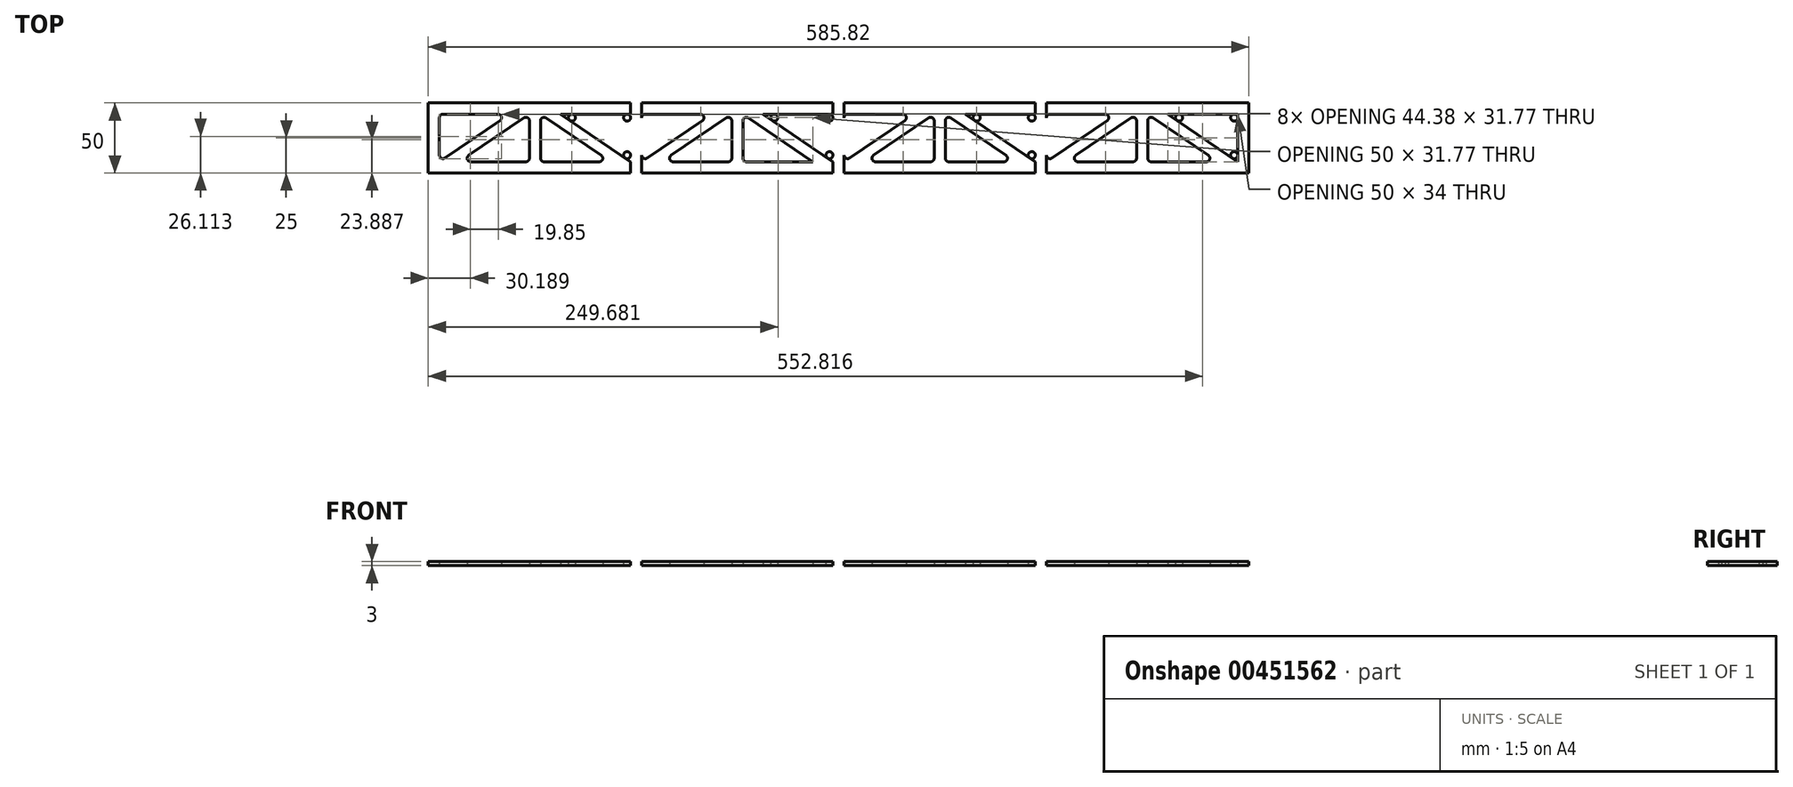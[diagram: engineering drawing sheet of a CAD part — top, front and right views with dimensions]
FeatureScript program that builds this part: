
annotation { "Feature Type Name" : "Feature", "Feature Type Description" : "" }
export const myFeature = defineFeature(function(context is Context, id is Id, definition is map)
    precondition{}
    {
        {
            var Q0;
            Q0=qCreatedBy(makeId("Top.planeOp"),FACE);
            var sketch = newSketch(context, id + "F0", { "sketchPlane" : qUnion([Q0])});
            skLineSegment(sketch, "E0.bottom", {"start": v(0, 0) * mm, "end": v(76.23, 0) * mm});
            skLineSegment(sketch, "E0.top", {"start": v(0, -50) * mm, "end": v(76.23, -50) * mm});
            skLineSegment(sketch, "E0.left", {"start": v(0, 0) * mm, "end": v(0, -50) * mm});
            skLineSegment(sketch, "E0.right", {"start": v(76.23, 0) * mm, "end": v(76.23, -50) * mm});
            skLineSegment(sketch, "E1", {"start": v(8, -8) * mm, "end": v(58, -8) * mm});
            skLineSegment(sketch, "E2", {"start": v(58, -8) * mm, "end": v(8, -42) * mm});
            skLineSegment(sketch, "E3", {"start": v(8, -42) * mm, "end": v(8, -8) * mm});
            skCircle(sketch, "E4", {"center": v(49.88, -10.5) * mm, "radius": 2.5 * mm});
            skCircle(sketch, "E5", {"center": v(10.5, -10.5) * mm, "radius": 2.5 * mm});
            skCircle(sketch, "E6", {"center": v(10.5, -37.28) * mm, "radius": 2.5 * mm});
            skLineSegment(sketch, "E7.MirrorCS", {"start": v(72.23, -8) * mm, "end": v(22.23, -42) * mm});
            skCircle(sketch, "E8.MirrorC", {"center": v(69.73, -12.72) * mm, "radius": 2.5 * mm});
            skLineSegment(sketch, "E9.MirrorCS", {"start": v(72.23, -42) * mm, "end": v(72.23, -8) * mm});
            skCircle(sketch, "E10.MirrorC", {"center": v(69.73, -39.5) * mm, "radius": 2.5 * mm});
            skCircle(sketch, "E11.MirrorC", {"center": v(30.35, -39.5) * mm, "radius": 2.5 * mm});
            skLineSegment(sketch, "E12.MirrorCS", {"start": v(22.23, -42) * mm, "end": v(72.23, -42) * mm});
            skCircle(sketch, "E13.MirrorC", {"center": v(141.95, -10.5) * mm, "radius": 2.5 * mm});
            skCircle(sketch, "E14.MirrorC", {"center": v(102.58, -10.5) * mm, "radius": 2.5 * mm});
            skCircle(sketch, "E15.MirrorC", {"center": v(141.95, -37.28) * mm, "radius": 2.5 * mm});
            skLineSegment(sketch, "E16.MirrorCS", {"start": v(144.45, -42) * mm, "end": v(144.45, -8) * mm});
            skLineSegment(sketch, "E17.MirrorCS", {"start": v(94.45, -8) * mm, "end": v(144.45, -42) * mm});
            skLineSegment(sketch, "E18.MirrorCS", {"start": v(144.45, -8) * mm, "end": v(94.45, -8) * mm});
            skCircle(sketch, "E19.MirrorC", {"center": v(82.73, -12.72) * mm, "radius": 2.5 * mm});
            skLineSegment(sketch, "E20.MirrorCS", {"start": v(130.23, -42) * mm, "end": v(80.23, -42) * mm});
            skLineSegment(sketch, "E21.MirrorCS", {"start": v(80.23, -8) * mm, "end": v(130.23, -42) * mm});
            skLineSegment(sketch, "E22.MirrorCS", {"start": v(152.45, 0) * mm, "end": v(152.45, -50) * mm});
            skCircle(sketch, "E23.MirrorC", {"center": v(82.73, -39.5) * mm, "radius": 2.5 * mm});
            skCircle(sketch, "E24.MirrorC", {"center": v(122.1, -39.5) * mm, "radius": 2.5 * mm});
            skLineSegment(sketch, "E25.MirrorCS", {"start": v(80.23, -42) * mm, "end": v(80.23, -8) * mm});
            skLineSegment(sketch, "E26.MirrorCS", {"start": v(152.45, -50) * mm, "end": v(76.23, -50) * mm});
            skLineSegment(sketch, "E27.MirrorCS", {"start": v(152.45, 0) * mm, "end": v(76.23, 0) * mm});
            skLineSegment(sketch, "E28.bottom", {"start": v(144.45, 0) * mm, "end": v(220.68, 0) * mm});
            skLineSegment(sketch, "E28.top", {"start": v(144.45, -50) * mm, "end": v(220.68, -50) * mm});
            skLineSegment(sketch, "E28.left", {"start": v(144.45, 0) * mm, "end": v(144.45, -50) * mm});
            skLineSegment(sketch, "E28.right", {"start": v(220.68, 0) * mm, "end": v(220.68, -50) * mm});
            skLineSegment(sketch, "E29", {"start": v(152.45, -8) * mm, "end": v(202.45, -8) * mm});
            skLineSegment(sketch, "E30", {"start": v(202.45, -8) * mm, "end": v(152.45, -42) * mm});
            skLineSegment(sketch, "E31", {"start": v(152.45, -42) * mm, "end": v(152.45, -8) * mm});
            skCircle(sketch, "E32", {"center": v(194.33, -10.5) * mm, "radius": 2.5 * mm});
            skCircle(sketch, "E33", {"center": v(154.95, -10.5) * mm, "radius": 2.5 * mm});
            skCircle(sketch, "E34", {"center": v(154.95, -37.28) * mm, "radius": 2.5 * mm});
            skLineSegment(sketch, "E35.MirrorCS", {"start": v(216.68, -8) * mm, "end": v(166.68, -42) * mm});
            skCircle(sketch, "E36.MirrorC", {"center": v(214.18, -12.72) * mm, "radius": 2.5 * mm});
            skLineSegment(sketch, "E37.MirrorCS", {"start": v(216.68, -42) * mm, "end": v(216.68, -8) * mm});
            skCircle(sketch, "E38.MirrorC", {"center": v(214.18, -39.5) * mm, "radius": 2.5 * mm});
            skCircle(sketch, "E39.MirrorC", {"center": v(174.8, -39.5) * mm, "radius": 2.5 * mm});
            skLineSegment(sketch, "E40.MirrorCS", {"start": v(166.68, -42) * mm, "end": v(216.68, -42) * mm});
            skCircle(sketch, "E41.MirrorC", {"center": v(286.4, -10.5) * mm, "radius": 2.5 * mm});
            skCircle(sketch, "E42.MirrorC", {"center": v(247.03, -10.5) * mm, "radius": 2.5 * mm});
            skCircle(sketch, "E43.MirrorC", {"center": v(286.4, -37.28) * mm, "radius": 2.5 * mm});
            skLineSegment(sketch, "E44.MirrorCS", {"start": v(288.9, -42) * mm, "end": v(288.9, -8) * mm});
            skLineSegment(sketch, "E45.MirrorCS", {"start": v(238.9, -8) * mm, "end": v(288.9, -42) * mm});
            skLineSegment(sketch, "E46.MirrorCS", {"start": v(288.9, -8) * mm, "end": v(238.9, -8) * mm});
            skCircle(sketch, "E47.MirrorC", {"center": v(227.18, -12.72) * mm, "radius": 2.5 * mm});
            skLineSegment(sketch, "E48.MirrorCS", {"start": v(274.68, -42) * mm, "end": v(224.68, -42) * mm});
            skLineSegment(sketch, "E49.MirrorCS", {"start": v(224.68, -8) * mm, "end": v(274.68, -42) * mm});
            skLineSegment(sketch, "E50.MirrorCS", {"start": v(296.9, 0) * mm, "end": v(296.9, -50) * mm});
            skCircle(sketch, "E51.MirrorC", {"center": v(227.18, -39.5) * mm, "radius": 2.5 * mm});
            skCircle(sketch, "E52.MirrorC", {"center": v(266.56, -39.5) * mm, "radius": 2.5 * mm});
            skLineSegment(sketch, "E53.MirrorCS", {"start": v(224.68, -42) * mm, "end": v(224.68, -8) * mm});
            skLineSegment(sketch, "E54.MirrorCS", {"start": v(296.9, -50) * mm, "end": v(220.68, -50) * mm});
            skLineSegment(sketch, "E55.MirrorCS", {"start": v(296.9, 0) * mm, "end": v(220.68, 0) * mm});
            skLineSegment(sketch, "E56.bottom", {"start": v(288.9, 0) * mm, "end": v(365.14, 0) * mm});
            skLineSegment(sketch, "E56.top", {"start": v(288.9, -50) * mm, "end": v(365.14, -50) * mm});
            skLineSegment(sketch, "E56.left", {"start": v(288.9, 0) * mm, "end": v(288.9, -50) * mm});
            skLineSegment(sketch, "E56.right", {"start": v(365.14, 0) * mm, "end": v(365.14, -50) * mm});
            skLineSegment(sketch, "E57", {"start": v(296.9, -8) * mm, "end": v(346.9, -8) * mm});
            skLineSegment(sketch, "E58", {"start": v(346.9, -8) * mm, "end": v(296.9, -42) * mm});
            skLineSegment(sketch, "E59", {"start": v(296.9, -42) * mm, "end": v(296.9, -8) * mm});
            skCircle(sketch, "E60", {"center": v(338.79, -10.5) * mm, "radius": 2.5 * mm});
            skCircle(sketch, "E61", {"center": v(299.4, -10.5) * mm, "radius": 2.5 * mm});
            skCircle(sketch, "E62", {"center": v(299.4, -37.28) * mm, "radius": 2.5 * mm});
            skLineSegment(sketch, "E63.MirrorCS", {"start": v(361.14, -8) * mm, "end": v(311.14, -42) * mm});
            skCircle(sketch, "E64.MirrorC", {"center": v(358.64, -12.72) * mm, "radius": 2.5 * mm});
            skLineSegment(sketch, "E65.MirrorCS", {"start": v(361.14, -42) * mm, "end": v(361.14, -8) * mm});
            skCircle(sketch, "E66.MirrorC", {"center": v(358.64, -39.5) * mm, "radius": 2.5 * mm});
            skCircle(sketch, "E67.MirrorC", {"center": v(319.26, -39.5) * mm, "radius": 2.5 * mm});
            skLineSegment(sketch, "E68.MirrorCS", {"start": v(311.14, -42) * mm, "end": v(361.14, -42) * mm});
            skCircle(sketch, "E69.MirrorC", {"center": v(430.86, -10.5) * mm, "radius": 2.5 * mm});
            skCircle(sketch, "E70.MirrorC", {"center": v(391.48, -10.5) * mm, "radius": 2.5 * mm});
            skCircle(sketch, "E71.MirrorC", {"center": v(430.86, -37.28) * mm, "radius": 2.5 * mm});
            skLineSegment(sketch, "E72.MirrorCS", {"start": v(433.36, -42) * mm, "end": v(433.36, -8) * mm});
            skLineSegment(sketch, "E73.MirrorCS", {"start": v(383.36, -8) * mm, "end": v(433.36, -42) * mm});
            skLineSegment(sketch, "E74.MirrorCS", {"start": v(433.36, -8) * mm, "end": v(383.36, -8) * mm});
            skCircle(sketch, "E75.MirrorC", {"center": v(371.64, -12.72) * mm, "radius": 2.5 * mm});
            skLineSegment(sketch, "E76.MirrorCS", {"start": v(419.14, -42) * mm, "end": v(369.14, -42) * mm});
            skLineSegment(sketch, "E77.MirrorCS", {"start": v(369.14, -8) * mm, "end": v(419.14, -42) * mm});
            skLineSegment(sketch, "E78.MirrorCS", {"start": v(441.36, 0) * mm, "end": v(441.36, -50) * mm});
            skCircle(sketch, "E79.MirrorC", {"center": v(371.64, -39.5) * mm, "radius": 2.5 * mm});
            skCircle(sketch, "E80.MirrorC", {"center": v(411.01, -39.5) * mm, "radius": 2.5 * mm});
            skLineSegment(sketch, "E81.MirrorCS", {"start": v(369.14, -42) * mm, "end": v(369.14, -8) * mm});
            skLineSegment(sketch, "E82.MirrorCS", {"start": v(441.36, -50) * mm, "end": v(365.14, -50) * mm});
            skLineSegment(sketch, "E83.MirrorCS", {"start": v(441.36, 0) * mm, "end": v(365.14, 0) * mm});
            skLineSegment(sketch, "E84.bottom", {"start": v(433.36, 0) * mm, "end": v(509.59, 0) * mm});
            skLineSegment(sketch, "E84.top", {"start": v(433.36, -50) * mm, "end": v(509.59, -50) * mm});
            skLineSegment(sketch, "E84.left", {"start": v(433.36, 0) * mm, "end": v(433.36, -50) * mm});
            skLineSegment(sketch, "E84.right", {"start": v(509.59, 0) * mm, "end": v(509.59, -50) * mm});
            skLineSegment(sketch, "E85", {"start": v(441.36, -8) * mm, "end": v(491.36, -8) * mm});
            skLineSegment(sketch, "E86", {"start": v(491.36, -8) * mm, "end": v(441.36, -42) * mm});
            skLineSegment(sketch, "E87", {"start": v(441.36, -42) * mm, "end": v(441.36, -8) * mm});
            skCircle(sketch, "E88", {"center": v(483.24, -10.5) * mm, "radius": 2.5 * mm});
            skCircle(sketch, "E89", {"center": v(443.86, -10.5) * mm, "radius": 2.5 * mm});
            skCircle(sketch, "E90", {"center": v(443.86, -37.28) * mm, "radius": 2.5 * mm});
            skLineSegment(sketch, "E91.MirrorCS", {"start": v(505.59, -8) * mm, "end": v(455.59, -42) * mm});
            skCircle(sketch, "E92.MirrorC", {"center": v(503.09, -12.72) * mm, "radius": 2.5 * mm});
            skLineSegment(sketch, "E93.MirrorCS", {"start": v(505.59, -42) * mm, "end": v(505.59, -8) * mm});
            skCircle(sketch, "E94.MirrorC", {"center": v(503.09, -39.5) * mm, "radius": 2.5 * mm});
            skCircle(sketch, "E95.MirrorC", {"center": v(463.71, -39.5) * mm, "radius": 2.5 * mm});
            skLineSegment(sketch, "E96.MirrorCS", {"start": v(455.59, -42) * mm, "end": v(505.59, -42) * mm});
            skCircle(sketch, "E97.MirrorC", {"center": v(575.32, -10.5) * mm, "radius": 2.5 * mm});
            skCircle(sketch, "E98.MirrorC", {"center": v(535.94, -10.5) * mm, "radius": 2.5 * mm});
            skCircle(sketch, "E99.MirrorC", {"center": v(575.32, -37.28) * mm, "radius": 2.5 * mm});
            skLineSegment(sketch, "E100.MirrorCS", {"start": v(577.82, -42) * mm, "end": v(577.82, -8) * mm});
            skLineSegment(sketch, "E101.MirrorCS", {"start": v(527.82, -8) * mm, "end": v(577.82, -42) * mm});
            skLineSegment(sketch, "E102.MirrorCS", {"start": v(577.82, -8) * mm, "end": v(527.82, -8) * mm});
            skCircle(sketch, "E103.MirrorC", {"center": v(516.09, -12.72) * mm, "radius": 2.5 * mm});
            skLineSegment(sketch, "E104.MirrorCS", {"start": v(563.59, -42) * mm, "end": v(513.59, -42) * mm});
            skLineSegment(sketch, "E105.MirrorCS", {"start": v(513.59, -8) * mm, "end": v(563.59, -42) * mm});
            skLineSegment(sketch, "E106.MirrorCS", {"start": v(585.82, 0) * mm, "end": v(585.82, -50) * mm});
            skCircle(sketch, "E107.MirrorC", {"center": v(516.09, -39.5) * mm, "radius": 2.5 * mm});
            skCircle(sketch, "E108.MirrorC", {"center": v(555.47, -39.5) * mm, "radius": 2.5 * mm});
            skLineSegment(sketch, "E109.MirrorCS", {"start": v(513.59, -42) * mm, "end": v(513.59, -8) * mm});
            skLineSegment(sketch, "E110.MirrorCS", {"start": v(585.82, -50) * mm, "end": v(509.59, -50) * mm});
            skLineSegment(sketch, "E111.MirrorCS", {"start": v(585.82, 0) * mm, "end": v(509.59, 0) * mm});
            skSolve(sketch);
        }
        {
            var Q0;
            Q0=makeQuery(id+"F0.imprint","IMPRINT",FACE,{"disambiguationData":[TD([[makeQuery(id+"F0.imprint","IMPRINT",EDGE,{"derivedFrom":sQuery(id+"F0.wireOp",EDGE,"E0.right")}),1.0]])]});
            var Q1;
            Q1=makeQuery(id+"F0.imprint","IMPRINT",FACE,{"disambiguationData":[TD([[makeQuery(id+"F0.imprint","IMPRINT",EDGE,{"derivedFrom":sQuery(id+"F0.wireOp",EDGE,"E0.bottom")}),-1.0]])]});
            var Q2;
            {var subQ0=sQuery(id+"F0.wireOp",EDGE,"E16.MirrorCS");var subQ1=sQuery(id+"F0.wireOp",EDGE,"E13.MirrorC");var subQ2=makeQuery(id+"F0.imprint","INTERSECT",VERTEX,{"derivedFrom":[subQ1,subQ0]});Q2=makeQuery(id+"F0.imprint","IMPRINT",FACE,{"disambiguationData":[TD([[makeQuery(id+"F0.imprint","IMPRINT",EDGE,{"disambiguationData":[TD([[subQ2,1.0]])],"derivedFrom":subQ1}),1.0]])]});}
            var Q3;
            {var subQ0=sQuery(id+"F0.wireOp",EDGE,"E16.MirrorCS");var subQ1=sQuery(id+"F0.wireOp",EDGE,"E15.MirrorC");var subQ2=makeQuery(id+"F0.imprint","INTERSECT",VERTEX,{"derivedFrom":[subQ1,subQ0]});Q3=makeQuery(id+"F0.imprint","IMPRINT",FACE,{"disambiguationData":[TD([[makeQuery(id+"F0.imprint","IMPRINT",EDGE,{"disambiguationData":[TD([[subQ2,-1.0]])],"derivedFrom":subQ1}),1.0]])]});}
            var Q4;
            {var subQ0=sQuery(id+"F0.wireOp",EDGE,"E21.MirrorCS");var subQ1=sQuery(id+"F0.wireOp",EDGE,"E20.MirrorCS");var subQ2=makeQuery(id+"F0.imprint","INTERSECT",VERTEX,{"derivedFrom":[subQ1,subQ0]});Q4=makeQuery(id+"F0.imprint","IMPRINT",FACE,{"disambiguationData":[TD([[makeQuery(id+"F0.imprint","IMPRINT",EDGE,{"disambiguationData":[TD([[subQ2,-1.0]])],"derivedFrom":subQ1}),-1.0]])]});}
            var Q5;
            {var subQ0=sQuery(id+"F0.wireOp",EDGE,"E25.MirrorCS");var subQ1=sQuery(id+"F0.wireOp",EDGE,"E20.MirrorCS");var subQ2=makeQuery(id+"F0.imprint","INTERSECT",VERTEX,{"derivedFrom":[subQ1,subQ0]});Q5=makeQuery(id+"F0.imprint","IMPRINT",FACE,{"disambiguationData":[TD([[makeQuery(id+"F0.imprint","IMPRINT",EDGE,{"disambiguationData":[TD([[subQ2,1.0]])],"derivedFrom":subQ1}),-1.0]])]});}
            var Q6;
            {var subQ0=sQuery(id+"F0.wireOp",EDGE,"E21.MirrorCS");var subQ1=sQuery(id+"F0.wireOp",EDGE,"E19.MirrorC");var subQ2=makeQuery(id+"F0.imprint","INTERSECT",VERTEX,{"derivedFrom":[subQ1,subQ0]});Q6=makeQuery(id+"F0.imprint","IMPRINT",FACE,{"disambiguationData":[TD([[makeQuery(id+"F0.imprint","IMPRINT",EDGE,{"disambiguationData":[TD([[subQ2,-1.0]])],"derivedFrom":subQ1}),-1.0]])]});}
            var Q7;
            {var subQ0=sQuery(id+"F0.wireOp",EDGE,"E17.MirrorCS");var subQ1=sQuery(id+"F0.wireOp",EDGE,"E14.MirrorC");var subQ2=makeQuery(id+"F0.imprint","INTERSECT",VERTEX,{"derivedFrom":[subQ1,subQ0]});Q7=makeQuery(id+"F0.imprint","IMPRINT",FACE,{"disambiguationData":[TD([[makeQuery(id+"F0.imprint","IMPRINT",EDGE,{"disambiguationData":[TD([[subQ2,-1.0]])],"derivedFrom":subQ1}),1.0]])]});}
            var Q8;
            {var subQ0=sQuery(id+"F0.wireOp",EDGE,"E3");var subQ1=sQuery(id+"F0.wireOp",EDGE,"E1");var subQ2=makeQuery(id+"F0.imprint","INTERSECT",VERTEX,{"derivedFrom":[subQ1,subQ0]});Q8=makeQuery(id+"F0.imprint","IMPRINT",FACE,{"disambiguationData":[TD([[makeQuery(id+"F0.imprint","IMPRINT",EDGE,{"disambiguationData":[TD([[subQ2,-1.0]])],"derivedFrom":subQ1}),-1.0]])]});}
            var Q9;
            {var subQ0=sQuery(id+"F0.wireOp",EDGE,"E3");var subQ1=sQuery(id+"F0.wireOp",EDGE,"E2");var subQ2=makeQuery(id+"F0.imprint","INTERSECT",VERTEX,{"derivedFrom":[subQ1,subQ0]});Q9=makeQuery(id+"F0.imprint","IMPRINT",FACE,{"disambiguationData":[TD([[makeQuery(id+"F0.imprint","IMPRINT",EDGE,{"disambiguationData":[TD([[subQ2,1.0]])],"derivedFrom":subQ1}),-1.0]])]});}
            var Q10;
            {var subQ0=sQuery(id+"F0.wireOp",EDGE,"E12.MirrorCS");var subQ1=sQuery(id+"F0.wireOp",EDGE,"E7.MirrorCS");var subQ2=makeQuery(id+"F0.imprint","INTERSECT",VERTEX,{"derivedFrom":[subQ1,subQ0]});Q10=makeQuery(id+"F0.imprint","IMPRINT",FACE,{"disambiguationData":[TD([[makeQuery(id+"F0.imprint","IMPRINT",EDGE,{"disambiguationData":[TD([[subQ2,1.0]])],"derivedFrom":subQ1}),1.0]])]});}
            var Q11;
            {var subQ0=sQuery(id+"F0.wireOp",EDGE,"E12.MirrorCS");var subQ1=sQuery(id+"F0.wireOp",EDGE,"E9.MirrorCS");var subQ2=makeQuery(id+"F0.imprint","INTERSECT",VERTEX,{"derivedFrom":[subQ1,subQ0]});Q11=makeQuery(id+"F0.imprint","IMPRINT",FACE,{"disambiguationData":[TD([[makeQuery(id+"F0.imprint","IMPRINT",EDGE,{"disambiguationData":[TD([[subQ2,-1.0]])],"derivedFrom":subQ1}),1.0]])]});}
            var Q12;
            {var subQ0=sQuery(id+"F0.wireOp",EDGE,"E9.MirrorCS");var subQ1=sQuery(id+"F0.wireOp",EDGE,"E7.MirrorCS");var subQ2=makeQuery(id+"F0.imprint","INTERSECT",VERTEX,{"derivedFrom":[subQ1,subQ0]});Q12=makeQuery(id+"F0.imprint","IMPRINT",FACE,{"disambiguationData":[TD([[makeQuery(id+"F0.imprint","IMPRINT",EDGE,{"disambiguationData":[TD([[subQ2,-1.0]])],"derivedFrom":subQ1}),1.0]])]});}
            var Q13;
            {var subQ0=sQuery(id+"F0.wireOp",EDGE,"E2");var subQ1=sQuery(id+"F0.wireOp",EDGE,"E1");var subQ2=makeQuery(id+"F0.imprint","INTERSECT",VERTEX,{"derivedFrom":[subQ1,subQ0]});Q13=makeQuery(id+"F0.imprint","IMPRINT",FACE,{"disambiguationData":[TD([[makeQuery(id+"F0.imprint","IMPRINT",EDGE,{"disambiguationData":[TD([[subQ2,1.0]])],"derivedFrom":subQ1}),-1.0]])]});}
            var Q14;
            Q14=makeQuery(id+"F0.imprint","IMPRINT",FACE,{"disambiguationData":[TD([[makeQuery(id+"F0.imprint","IMPRINT",EDGE,{"derivedFrom":sQuery(id+"F0.wireOp",EDGE,"9c0d0d47-12da-48a8-bd43-616823d97947.bottom")}),-1.0]])]});
            var Q15;
            Q15=makeQuery(id+"F0.imprint","IMPRINT",FACE,{"disambiguationData":[TD([[makeQuery(id+"F0.imprint","IMPRINT",EDGE,{"derivedFrom":sQuery(id+"F0.wireOp",EDGE,"9c0d0d47-12da-48a8-bd43-616823d97947.right")}),1.0]])]});
            var Q16;
            {var subQ0=sQuery(id+"F0.wireOp",EDGE,"47e6eebe-d896-4bef-a27f-de648a51b396.MirrorCS");var subQ1=sQuery(id+"F0.wireOp",EDGE,"eb915fa9-9426-4ec2-aa22-30cccfdd8270.MirrorC");var subQ2=makeQuery(id+"F0.imprint","INTERSECT",VERTEX,{"derivedFrom":[subQ1,subQ0]});Q16=makeQuery(id+"F0.imprint","IMPRINT",FACE,{"disambiguationData":[TD([[makeQuery(id+"F0.imprint","IMPRINT",EDGE,{"disambiguationData":[TD([[subQ2,-1.0]])],"derivedFrom":subQ1}),1.0]])]});}
            var Q17;
            {var subQ0=sQuery(id+"F0.wireOp",EDGE,"e0770472-00ef-4bcc-97a7-d35b8869f1f1.MirrorCS");var subQ1=sQuery(id+"F0.wireOp",EDGE,"2073ca2d-185e-4dbb-aacc-5a1a50917c44.MirrorC");var subQ2=makeQuery(id+"F0.imprint","INTERSECT",VERTEX,{"derivedFrom":[subQ1,subQ0]});Q17=makeQuery(id+"F0.imprint","IMPRINT",FACE,{"disambiguationData":[TD([[makeQuery(id+"F0.imprint","IMPRINT",EDGE,{"disambiguationData":[TD([[subQ2,-1.0]])],"derivedFrom":subQ1}),1.0]])]});}
            var Q18;
            {var subQ0=sQuery(id+"F0.wireOp",EDGE,"adea8092-a6c0-4993-8707-dc8c8bcecc7c.MirrorCS");var subQ1=sQuery(id+"F0.wireOp",EDGE,"a41aebc5-1699-424e-9aee-a3a47674efbf.MirrorCS");var subQ2=makeQuery(id+"F0.imprint","INTERSECT",VERTEX,{"derivedFrom":[subQ1,subQ0]});Q18=makeQuery(id+"F0.imprint","IMPRINT",FACE,{"disambiguationData":[TD([[makeQuery(id+"F0.imprint","IMPRINT",EDGE,{"disambiguationData":[TD([[subQ2,-1.0]])],"derivedFrom":subQ1}),-1.0]])]});}
            var Q19;
            {var subQ0=sQuery(id+"F0.wireOp",EDGE,"adea8092-a6c0-4993-8707-dc8c8bcecc7c.MirrorCS");var subQ1=sQuery(id+"F0.wireOp",EDGE,"d0978fc5-0042-4f22-8c9f-83e4bf24dd17.MirrorC");var subQ2=makeQuery(id+"F0.imprint","INTERSECT",VERTEX,{"derivedFrom":[subQ1,subQ0]});Q19=makeQuery(id+"F0.imprint","IMPRINT",FACE,{"disambiguationData":[TD([[makeQuery(id+"F0.imprint","IMPRINT",EDGE,{"disambiguationData":[TD([[subQ2,-1.0]])],"derivedFrom":subQ1}),-1.0]])]});}
            var Q20;
            {var subQ0=sQuery(id+"F0.wireOp",EDGE,"03bcc0c7-1de4-4aa4-b49b-c102c2159368.MirrorCS");var subQ1=sQuery(id+"F0.wireOp",EDGE,"84b653b7-858e-4f8b-98a3-bff0c21978d8.MirrorCS");var subQ2=makeQuery(id+"F0.imprint","INTERSECT",VERTEX,{"derivedFrom":[subQ1,subQ0]});Q20=makeQuery(id+"F0.imprint","IMPRINT",FACE,{"disambiguationData":[TD([[makeQuery(id+"F0.imprint","IMPRINT",EDGE,{"disambiguationData":[TD([[subQ2,-1.0]])],"derivedFrom":subQ1}),1.0]])]});}
            var Q21;
            {var subQ0=sQuery(id+"F0.wireOp",EDGE,"882f1e57-158f-4c4e-b2c3-cdc22070b6c0");var subQ1=sQuery(id+"F0.wireOp",EDGE,"3fc96e6c-2ba4-4e3e-bb61-cf4d3951b191");var subQ2=makeQuery(id+"F0.imprint","INTERSECT",VERTEX,{"derivedFrom":[subQ1,subQ0]});Q21=makeQuery(id+"F0.imprint","IMPRINT",FACE,{"disambiguationData":[TD([[makeQuery(id+"F0.imprint","IMPRINT",EDGE,{"disambiguationData":[TD([[subQ2,1.0]])],"derivedFrom":subQ1}),-1.0]])]});}
            var Q22;
            {var subQ0=sQuery(id+"F0.wireOp",EDGE,"5e04dc24-51b3-488f-bbf6-ceb28c03ea6f");var subQ1=sQuery(id+"F0.wireOp",EDGE,"882f1e57-158f-4c4e-b2c3-cdc22070b6c0");var subQ2=makeQuery(id+"F0.imprint","INTERSECT",VERTEX,{"derivedFrom":[subQ1,subQ0]});Q22=makeQuery(id+"F0.imprint","IMPRINT",FACE,{"disambiguationData":[TD([[makeQuery(id+"F0.imprint","IMPRINT",EDGE,{"disambiguationData":[TD([[subQ2,1.0]])],"derivedFrom":subQ1}),-1.0]])]});}
            var Q23;
            {var subQ0=sQuery(id+"F0.wireOp",EDGE,"f8bb7a45-0dee-45f7-9e24-93a754e4dec8.MirrorCS");var subQ1=sQuery(id+"F0.wireOp",EDGE,"84b653b7-858e-4f8b-98a3-bff0c21978d8.MirrorCS");var subQ2=makeQuery(id+"F0.imprint","INTERSECT",VERTEX,{"derivedFrom":[subQ1,subQ0]});Q23=makeQuery(id+"F0.imprint","IMPRINT",FACE,{"disambiguationData":[TD([[makeQuery(id+"F0.imprint","IMPRINT",EDGE,{"disambiguationData":[TD([[subQ2,1.0]])],"derivedFrom":subQ1}),1.0]])]});}
            var Q24;
            {var subQ0=sQuery(id+"F0.wireOp",EDGE,"5e04dc24-51b3-488f-bbf6-ceb28c03ea6f");var subQ1=sQuery(id+"F0.wireOp",EDGE,"3fc96e6c-2ba4-4e3e-bb61-cf4d3951b191");var subQ2=makeQuery(id+"F0.imprint","INTERSECT",VERTEX,{"derivedFrom":[subQ1,subQ0]});Q24=makeQuery(id+"F0.imprint","IMPRINT",FACE,{"disambiguationData":[TD([[makeQuery(id+"F0.imprint","IMPRINT",EDGE,{"disambiguationData":[TD([[subQ2,-1.0]])],"derivedFrom":subQ1}),-1.0]])]});}
            var Q25;
            {var subQ0=sQuery(id+"F0.wireOp",EDGE,"f8bb7a45-0dee-45f7-9e24-93a754e4dec8.MirrorCS");var subQ1=sQuery(id+"F0.wireOp",EDGE,"03bcc0c7-1de4-4aa4-b49b-c102c2159368.MirrorCS");var subQ2=makeQuery(id+"F0.imprint","INTERSECT",VERTEX,{"derivedFrom":[subQ1,subQ0]});Q25=makeQuery(id+"F0.imprint","IMPRINT",FACE,{"disambiguationData":[TD([[makeQuery(id+"F0.imprint","IMPRINT",EDGE,{"disambiguationData":[TD([[subQ2,-1.0]])],"derivedFrom":subQ1}),1.0]])]});}
            var Q26;
            {var subQ0=sQuery(id+"F0.wireOp",EDGE,"ffd879e6-b5cc-4603-a084-e9b53f592fdf.MirrorCS");var subQ1=sQuery(id+"F0.wireOp",EDGE,"a41aebc5-1699-424e-9aee-a3a47674efbf.MirrorCS");var subQ2=makeQuery(id+"F0.imprint","INTERSECT",VERTEX,{"derivedFrom":[subQ1,subQ0]});Q26=makeQuery(id+"F0.imprint","IMPRINT",FACE,{"disambiguationData":[TD([[makeQuery(id+"F0.imprint","IMPRINT",EDGE,{"disambiguationData":[TD([[subQ2,1.0]])],"derivedFrom":subQ1}),-1.0]])]});}
            var Q27;
            {var subQ0=sQuery(id+"F0.wireOp",EDGE,"e0770472-00ef-4bcc-97a7-d35b8869f1f1.MirrorCS");var subQ1=sQuery(id+"F0.wireOp",EDGE,"c4c67041-a6ca-4b6e-a7e7-0204011651bc.MirrorC");var subQ2=makeQuery(id+"F0.imprint","INTERSECT",VERTEX,{"derivedFrom":[subQ1,subQ0]});Q27=makeQuery(id+"F0.imprint","IMPRINT",FACE,{"disambiguationData":[TD([[makeQuery(id+"F0.imprint","IMPRINT",EDGE,{"disambiguationData":[TD([[subQ2,1.0]])],"derivedFrom":subQ1}),1.0]])]});}
            var Q28;
            {var subQ0=sQuery(id+"F0.wireOp",EDGE,"E28.left");var subQ10=makeQuery(id+"F0.imprint","INTERSECT",VERTEX,{"derivedFrom":[sQuery(id+"F0.wireOp",EDGE,"E18.MirrorCS"),subQ0]});Q28=makeQuery(id+"F0.imprint","IMPRINT",FACE,{"disambiguationData":[TD([[makeQuery(id+"F0.imprint","IMPRINT",EDGE,{"disambiguationData":[TD([[subQ10,-1.0]])],"derivedFrom":subQ0}),1.0]])]});}
            var Q29;
            {var subQ12=sQuery(id+"F0.wireOp",EDGE,"E28.right");Q29=makeQuery(id+"F0.imprint","IMPRINT",FACE,{"disambiguationData":[TD([[makeQuery(id+"F0.imprint","IMPRINT",EDGE,{"derivedFrom":subQ12}),-1.0]])]});}
            var Q30;
            Q30=makeQuery(id+"F0.imprint","IMPRINT",FACE,{"disambiguationData":[TD([[makeQuery(id+"F0.imprint","IMPRINT",EDGE,{"derivedFrom":sQuery(id+"F0.wireOp",EDGE,"E28.right")}),1.0]])]});
            var Q31;
            {var subQ12=sQuery(id+"F0.wireOp",EDGE,"E56.right");Q31=makeQuery(id+"F0.imprint","IMPRINT",FACE,{"disambiguationData":[TD([[makeQuery(id+"F0.imprint","IMPRINT",EDGE,{"derivedFrom":subQ12}),-1.0]])]});}
            var Q32;
            {var subQ0=sQuery(id+"F0.wireOp",EDGE,"E56.left");var subQ10=makeQuery(id+"F0.imprint","INTERSECT",VERTEX,{"derivedFrom":[sQuery(id+"F0.wireOp",EDGE,"E46.MirrorCS"),subQ0]});Q32=makeQuery(id+"F0.imprint","IMPRINT",FACE,{"disambiguationData":[TD([[makeQuery(id+"F0.imprint","IMPRINT",EDGE,{"disambiguationData":[TD([[subQ10,-1.0]])],"derivedFrom":subQ0}),1.0]])]});}
            var Q33;
            Q33=makeQuery(id+"F0.imprint","IMPRINT",FACE,{"disambiguationData":[TD([[makeQuery(id+"F0.imprint","IMPRINT",EDGE,{"derivedFrom":sQuery(id+"F0.wireOp",EDGE,"E56.right")}),1.0]])]});
            var Q34;
            {var subQ0=sQuery(id+"F0.wireOp",EDGE,"E84.left");var subQ10=makeQuery(id+"F0.imprint","INTERSECT",VERTEX,{"derivedFrom":[sQuery(id+"F0.wireOp",EDGE,"E74.MirrorCS"),subQ0]});Q34=makeQuery(id+"F0.imprint","IMPRINT",FACE,{"disambiguationData":[TD([[makeQuery(id+"F0.imprint","IMPRINT",EDGE,{"disambiguationData":[TD([[subQ10,-1.0]])],"derivedFrom":subQ0}),1.0]])]});}
            var Q35;
            {var subQ12=sQuery(id+"F0.wireOp",EDGE,"E84.right");Q35=makeQuery(id+"F0.imprint","IMPRINT",FACE,{"disambiguationData":[TD([[makeQuery(id+"F0.imprint","IMPRINT",EDGE,{"derivedFrom":subQ12}),-1.0]])]});}
            var Q36;
            Q36=makeQuery(id+"F0.imprint","IMPRINT",FACE,{"disambiguationData":[TD([[makeQuery(id+"F0.imprint","IMPRINT",EDGE,{"derivedFrom":sQuery(id+"F0.wireOp",EDGE,"E84.right")}),1.0]])]});
            var Q37;
            {var subQ1=sQuery(id+"F0.wireOp",EDGE,"E29");var subQ3=sQuery(id+"F0.wireOp",EDGE,"E33");var subQ4=makeQuery(id+"F0.imprint","INTERSECT",VERTEX,{"derivedFrom":[subQ1,subQ3]});Q37=makeQuery(id+"F0.imprint","IMPRINT",FACE,{"disambiguationData":[TD([[makeQuery(id+"F0.imprint","IMPRINT",EDGE,{"disambiguationData":[TD([[subQ4,-1.0]])],"derivedFrom":subQ3}),-1.0]])]});}
            var Q38;
            {var subQ1=sQuery(id+"F0.wireOp",EDGE,"E30");var subQ3=sQuery(id+"F0.wireOp",EDGE,"E34");var subQ4=makeQuery(id+"F0.imprint","INTERSECT",VERTEX,{"derivedFrom":[subQ1,subQ3]});Q38=makeQuery(id+"F0.imprint","IMPRINT",FACE,{"disambiguationData":[TD([[makeQuery(id+"F0.imprint","IMPRINT",EDGE,{"disambiguationData":[TD([[subQ4,1.0]])],"derivedFrom":subQ3}),-1.0]])]});}
            var Q39;
            {var subQ0=sQuery(id+"F0.wireOp",EDGE,"E30");var subQ1=sQuery(id+"F0.wireOp",EDGE,"E29");var subQ2=makeQuery(id+"F0.imprint","INTERSECT",VERTEX,{"derivedFrom":[subQ1,subQ0]});Q39=makeQuery(id+"F0.imprint","IMPRINT",FACE,{"disambiguationData":[TD([[makeQuery(id+"F0.imprint","IMPRINT",EDGE,{"disambiguationData":[TD([[subQ2,1.0]])],"derivedFrom":subQ1}),-1.0]])]});}
            var Q40;
            {var subQ0=sQuery(id+"F0.wireOp",EDGE,"E40.MirrorCS");var subQ1=sQuery(id+"F0.wireOp",EDGE,"E35.MirrorCS");var subQ2=makeQuery(id+"F0.imprint","INTERSECT",VERTEX,{"derivedFrom":[subQ1,subQ0]});Q40=makeQuery(id+"F0.imprint","IMPRINT",FACE,{"disambiguationData":[TD([[makeQuery(id+"F0.imprint","IMPRINT",EDGE,{"disambiguationData":[TD([[subQ2,1.0]])],"derivedFrom":subQ1}),1.0]])]});}
            var Q41;
            {var subQ0=sQuery(id+"F0.wireOp",EDGE,"E40.MirrorCS");var subQ1=sQuery(id+"F0.wireOp",EDGE,"E37.MirrorCS");var subQ2=makeQuery(id+"F0.imprint","INTERSECT",VERTEX,{"derivedFrom":[subQ1,subQ0]});Q41=makeQuery(id+"F0.imprint","IMPRINT",FACE,{"disambiguationData":[TD([[makeQuery(id+"F0.imprint","IMPRINT",EDGE,{"disambiguationData":[TD([[subQ2,-1.0]])],"derivedFrom":subQ1}),1.0]])]});}
            var Q42;
            {var subQ0=sQuery(id+"F0.wireOp",EDGE,"E37.MirrorCS");var subQ1=sQuery(id+"F0.wireOp",EDGE,"E35.MirrorCS");var subQ2=makeQuery(id+"F0.imprint","INTERSECT",VERTEX,{"derivedFrom":[subQ1,subQ0]});Q42=makeQuery(id+"F0.imprint","IMPRINT",FACE,{"disambiguationData":[TD([[makeQuery(id+"F0.imprint","IMPRINT",EDGE,{"disambiguationData":[TD([[subQ2,-1.0]])],"derivedFrom":subQ1}),1.0]])]});}
            var Q43;
            {var subQ0=sQuery(id+"F0.wireOp",EDGE,"E49.MirrorCS");var subQ1=sQuery(id+"F0.wireOp",EDGE,"E47.MirrorC");var subQ2=makeQuery(id+"F0.imprint","INTERSECT",VERTEX,{"derivedFrom":[subQ1,subQ0]});Q43=makeQuery(id+"F0.imprint","IMPRINT",FACE,{"disambiguationData":[TD([[makeQuery(id+"F0.imprint","IMPRINT",EDGE,{"disambiguationData":[TD([[subQ2,-1.0]])],"derivedFrom":subQ1}),-1.0]])]});}
            var Q44;
            {var subQ0=sQuery(id+"F0.wireOp",EDGE,"E53.MirrorCS");var subQ1=sQuery(id+"F0.wireOp",EDGE,"E48.MirrorCS");var subQ2=makeQuery(id+"F0.imprint","INTERSECT",VERTEX,{"derivedFrom":[subQ1,subQ0]});Q44=makeQuery(id+"F0.imprint","IMPRINT",FACE,{"disambiguationData":[TD([[makeQuery(id+"F0.imprint","IMPRINT",EDGE,{"disambiguationData":[TD([[subQ2,1.0]])],"derivedFrom":subQ1}),-1.0]])]});}
            var Q45;
            {var subQ0=sQuery(id+"F0.wireOp",EDGE,"E45.MirrorCS");var subQ1=sQuery(id+"F0.wireOp",EDGE,"E42.MirrorC");var subQ2=makeQuery(id+"F0.imprint","INTERSECT",VERTEX,{"derivedFrom":[subQ1,subQ0]});Q45=makeQuery(id+"F0.imprint","IMPRINT",FACE,{"disambiguationData":[TD([[makeQuery(id+"F0.imprint","IMPRINT",EDGE,{"disambiguationData":[TD([[subQ2,-1.0]])],"derivedFrom":subQ1}),1.0]])]});}
            var Q46;
            {var subQ0=sQuery(id+"F0.wireOp",EDGE,"E46.MirrorCS");var subQ1=sQuery(id+"F0.wireOp",EDGE,"E41.MirrorC");var subQ2=makeQuery(id+"F0.imprint","INTERSECT",VERTEX,{"derivedFrom":[subQ1,subQ0]});Q46=makeQuery(id+"F0.imprint","IMPRINT",FACE,{"disambiguationData":[TD([[makeQuery(id+"F0.imprint","IMPRINT",EDGE,{"disambiguationData":[TD([[subQ2,-1.0]])],"derivedFrom":subQ1}),1.0]])]});}
            var Q47;
            {var subQ0=sQuery(id+"F0.wireOp",EDGE,"E45.MirrorCS");var subQ1=sQuery(id+"F0.wireOp",EDGE,"E43.MirrorC");var subQ2=makeQuery(id+"F0.imprint","INTERSECT",VERTEX,{"derivedFrom":[subQ1,subQ0]});Q47=makeQuery(id+"F0.imprint","IMPRINT",FACE,{"disambiguationData":[TD([[makeQuery(id+"F0.imprint","IMPRINT",EDGE,{"disambiguationData":[TD([[subQ2,1.0]])],"derivedFrom":subQ1}),1.0]])]});}
            var Q48;
            {var subQ1=sQuery(id+"F0.wireOp",EDGE,"E58");var subQ3=sQuery(id+"F0.wireOp",EDGE,"E62");var subQ4=makeQuery(id+"F0.imprint","INTERSECT",VERTEX,{"derivedFrom":[subQ1,subQ3]});Q48=makeQuery(id+"F0.imprint","IMPRINT",FACE,{"disambiguationData":[TD([[makeQuery(id+"F0.imprint","IMPRINT",EDGE,{"disambiguationData":[TD([[subQ4,1.0]])],"derivedFrom":subQ3}),-1.0]])]});}
            var Q49;
            {var subQ1=sQuery(id+"F0.wireOp",EDGE,"E57");var subQ3=sQuery(id+"F0.wireOp",EDGE,"E61");var subQ4=makeQuery(id+"F0.imprint","INTERSECT",VERTEX,{"derivedFrom":[subQ1,subQ3]});Q49=makeQuery(id+"F0.imprint","IMPRINT",FACE,{"disambiguationData":[TD([[makeQuery(id+"F0.imprint","IMPRINT",EDGE,{"disambiguationData":[TD([[subQ4,-1.0]])],"derivedFrom":subQ3}),-1.0]])]});}
            var Q50;
            {var subQ0=sQuery(id+"F0.wireOp",EDGE,"E68.MirrorCS");var subQ1=sQuery(id+"F0.wireOp",EDGE,"E63.MirrorCS");var subQ2=makeQuery(id+"F0.imprint","INTERSECT",VERTEX,{"derivedFrom":[subQ1,subQ0]});Q50=makeQuery(id+"F0.imprint","IMPRINT",FACE,{"disambiguationData":[TD([[makeQuery(id+"F0.imprint","IMPRINT",EDGE,{"disambiguationData":[TD([[subQ2,1.0]])],"derivedFrom":subQ1}),1.0]])]});}
            var Q51;
            {var subQ0=sQuery(id+"F0.wireOp",EDGE,"E58");var subQ1=sQuery(id+"F0.wireOp",EDGE,"E57");var subQ2=makeQuery(id+"F0.imprint","INTERSECT",VERTEX,{"derivedFrom":[subQ1,subQ0]});Q51=makeQuery(id+"F0.imprint","IMPRINT",FACE,{"disambiguationData":[TD([[makeQuery(id+"F0.imprint","IMPRINT",EDGE,{"disambiguationData":[TD([[subQ2,1.0]])],"derivedFrom":subQ1}),-1.0]])]});}
            var Q52;
            {var subQ0=sQuery(id+"F0.wireOp",EDGE,"E65.MirrorCS");var subQ1=sQuery(id+"F0.wireOp",EDGE,"E63.MirrorCS");var subQ2=makeQuery(id+"F0.imprint","INTERSECT",VERTEX,{"derivedFrom":[subQ1,subQ0]});Q52=makeQuery(id+"F0.imprint","IMPRINT",FACE,{"disambiguationData":[TD([[makeQuery(id+"F0.imprint","IMPRINT",EDGE,{"disambiguationData":[TD([[subQ2,-1.0]])],"derivedFrom":subQ1}),1.0]])]});}
            var Q53;
            {var subQ0=sQuery(id+"F0.wireOp",EDGE,"E68.MirrorCS");var subQ1=sQuery(id+"F0.wireOp",EDGE,"E65.MirrorCS");var subQ2=makeQuery(id+"F0.imprint","INTERSECT",VERTEX,{"derivedFrom":[subQ1,subQ0]});Q53=makeQuery(id+"F0.imprint","IMPRINT",FACE,{"disambiguationData":[TD([[makeQuery(id+"F0.imprint","IMPRINT",EDGE,{"disambiguationData":[TD([[subQ2,-1.0]])],"derivedFrom":subQ1}),1.0]])]});}
            var Q54;
            {var subQ0=sQuery(id+"F0.wireOp",EDGE,"E81.MirrorCS");var subQ1=sQuery(id+"F0.wireOp",EDGE,"E76.MirrorCS");var subQ2=makeQuery(id+"F0.imprint","INTERSECT",VERTEX,{"derivedFrom":[subQ1,subQ0]});Q54=makeQuery(id+"F0.imprint","IMPRINT",FACE,{"disambiguationData":[TD([[makeQuery(id+"F0.imprint","IMPRINT",EDGE,{"disambiguationData":[TD([[subQ2,1.0]])],"derivedFrom":subQ1}),-1.0]])]});}
            var Q55;
            {var subQ0=sQuery(id+"F0.wireOp",EDGE,"E77.MirrorCS");var subQ1=sQuery(id+"F0.wireOp",EDGE,"E75.MirrorC");var subQ2=makeQuery(id+"F0.imprint","INTERSECT",VERTEX,{"derivedFrom":[subQ1,subQ0]});Q55=makeQuery(id+"F0.imprint","IMPRINT",FACE,{"disambiguationData":[TD([[makeQuery(id+"F0.imprint","IMPRINT",EDGE,{"disambiguationData":[TD([[subQ2,-1.0]])],"derivedFrom":subQ1}),-1.0]])]});}
            var Q56;
            {var subQ0=sQuery(id+"F0.wireOp",EDGE,"E77.MirrorCS");var subQ1=sQuery(id+"F0.wireOp",EDGE,"E76.MirrorCS");var subQ2=makeQuery(id+"F0.imprint","INTERSECT",VERTEX,{"derivedFrom":[subQ1,subQ0]});Q56=makeQuery(id+"F0.imprint","IMPRINT",FACE,{"disambiguationData":[TD([[makeQuery(id+"F0.imprint","IMPRINT",EDGE,{"disambiguationData":[TD([[subQ2,-1.0]])],"derivedFrom":subQ1}),-1.0]])]});}
            var Q57;
            {var subQ0=sQuery(id+"F0.wireOp",EDGE,"E73.MirrorCS");var subQ1=sQuery(id+"F0.wireOp",EDGE,"E70.MirrorC");var subQ2=makeQuery(id+"F0.imprint","INTERSECT",VERTEX,{"derivedFrom":[subQ1,subQ0]});Q57=makeQuery(id+"F0.imprint","IMPRINT",FACE,{"disambiguationData":[TD([[makeQuery(id+"F0.imprint","IMPRINT",EDGE,{"disambiguationData":[TD([[subQ2,-1.0]])],"derivedFrom":subQ1}),1.0]])]});}
            var Q58;
            {var subQ0=sQuery(id+"F0.wireOp",EDGE,"E74.MirrorCS");var subQ1=sQuery(id+"F0.wireOp",EDGE,"E69.MirrorC");var subQ2=makeQuery(id+"F0.imprint","INTERSECT",VERTEX,{"derivedFrom":[subQ1,subQ0]});Q58=makeQuery(id+"F0.imprint","IMPRINT",FACE,{"disambiguationData":[TD([[makeQuery(id+"F0.imprint","IMPRINT",EDGE,{"disambiguationData":[TD([[subQ2,-1.0]])],"derivedFrom":subQ1}),1.0]])]});}
            var Q59;
            {var subQ0=sQuery(id+"F0.wireOp",EDGE,"E73.MirrorCS");var subQ1=sQuery(id+"F0.wireOp",EDGE,"E71.MirrorC");var subQ2=makeQuery(id+"F0.imprint","INTERSECT",VERTEX,{"derivedFrom":[subQ1,subQ0]});Q59=makeQuery(id+"F0.imprint","IMPRINT",FACE,{"disambiguationData":[TD([[makeQuery(id+"F0.imprint","IMPRINT",EDGE,{"disambiguationData":[TD([[subQ2,1.0]])],"derivedFrom":subQ1}),1.0]])]});}
            var Q60;
            {var subQ1=sQuery(id+"F0.wireOp",EDGE,"E86");var subQ3=sQuery(id+"F0.wireOp",EDGE,"E90");var subQ4=makeQuery(id+"F0.imprint","INTERSECT",VERTEX,{"derivedFrom":[subQ1,subQ3]});Q60=makeQuery(id+"F0.imprint","IMPRINT",FACE,{"disambiguationData":[TD([[makeQuery(id+"F0.imprint","IMPRINT",EDGE,{"disambiguationData":[TD([[subQ4,1.0]])],"derivedFrom":subQ3}),-1.0]])]});}
            var Q61;
            {var subQ1=sQuery(id+"F0.wireOp",EDGE,"E85");var subQ3=sQuery(id+"F0.wireOp",EDGE,"E89");var subQ4=makeQuery(id+"F0.imprint","INTERSECT",VERTEX,{"derivedFrom":[subQ1,subQ3]});Q61=makeQuery(id+"F0.imprint","IMPRINT",FACE,{"disambiguationData":[TD([[makeQuery(id+"F0.imprint","IMPRINT",EDGE,{"disambiguationData":[TD([[subQ4,-1.0]])],"derivedFrom":subQ3}),-1.0]])]});}
            var Q62;
            {var subQ0=sQuery(id+"F0.wireOp",EDGE,"E96.MirrorCS");var subQ1=sQuery(id+"F0.wireOp",EDGE,"E91.MirrorCS");var subQ2=makeQuery(id+"F0.imprint","INTERSECT",VERTEX,{"derivedFrom":[subQ1,subQ0]});Q62=makeQuery(id+"F0.imprint","IMPRINT",FACE,{"disambiguationData":[TD([[makeQuery(id+"F0.imprint","IMPRINT",EDGE,{"disambiguationData":[TD([[subQ2,1.0]])],"derivedFrom":subQ1}),1.0]])]});}
            var Q63;
            {var subQ0=sQuery(id+"F0.wireOp",EDGE,"E86");var subQ1=sQuery(id+"F0.wireOp",EDGE,"E85");var subQ2=makeQuery(id+"F0.imprint","INTERSECT",VERTEX,{"derivedFrom":[subQ1,subQ0]});Q63=makeQuery(id+"F0.imprint","IMPRINT",FACE,{"disambiguationData":[TD([[makeQuery(id+"F0.imprint","IMPRINT",EDGE,{"disambiguationData":[TD([[subQ2,1.0]])],"derivedFrom":subQ1}),-1.0]])]});}
            var Q64;
            {var subQ0=sQuery(id+"F0.wireOp",EDGE,"E93.MirrorCS");var subQ1=sQuery(id+"F0.wireOp",EDGE,"E91.MirrorCS");var subQ2=makeQuery(id+"F0.imprint","INTERSECT",VERTEX,{"derivedFrom":[subQ1,subQ0]});Q64=makeQuery(id+"F0.imprint","IMPRINT",FACE,{"disambiguationData":[TD([[makeQuery(id+"F0.imprint","IMPRINT",EDGE,{"disambiguationData":[TD([[subQ2,-1.0]])],"derivedFrom":subQ1}),1.0]])]});}
            var Q65;
            {var subQ0=sQuery(id+"F0.wireOp",EDGE,"E96.MirrorCS");var subQ1=sQuery(id+"F0.wireOp",EDGE,"E93.MirrorCS");var subQ2=makeQuery(id+"F0.imprint","INTERSECT",VERTEX,{"derivedFrom":[subQ1,subQ0]});Q65=makeQuery(id+"F0.imprint","IMPRINT",FACE,{"disambiguationData":[TD([[makeQuery(id+"F0.imprint","IMPRINT",EDGE,{"disambiguationData":[TD([[subQ2,-1.0]])],"derivedFrom":subQ1}),1.0]])]});}
            var Q66;
            {var subQ0=sQuery(id+"F0.wireOp",EDGE,"E105.MirrorCS");var subQ1=sQuery(id+"F0.wireOp",EDGE,"E103.MirrorC");var subQ2=makeQuery(id+"F0.imprint","INTERSECT",VERTEX,{"derivedFrom":[subQ1,subQ0]});Q66=makeQuery(id+"F0.imprint","IMPRINT",FACE,{"disambiguationData":[TD([[makeQuery(id+"F0.imprint","IMPRINT",EDGE,{"disambiguationData":[TD([[subQ2,-1.0]])],"derivedFrom":subQ1}),-1.0]])]});}
            var Q67;
            {var subQ0=sQuery(id+"F0.wireOp",EDGE,"E109.MirrorCS");var subQ1=sQuery(id+"F0.wireOp",EDGE,"E104.MirrorCS");var subQ2=makeQuery(id+"F0.imprint","INTERSECT",VERTEX,{"derivedFrom":[subQ1,subQ0]});Q67=makeQuery(id+"F0.imprint","IMPRINT",FACE,{"disambiguationData":[TD([[makeQuery(id+"F0.imprint","IMPRINT",EDGE,{"disambiguationData":[TD([[subQ2,1.0]])],"derivedFrom":subQ1}),-1.0]])]});}
            var Q68;
            {var subQ0=sQuery(id+"F0.wireOp",EDGE,"E105.MirrorCS");var subQ1=sQuery(id+"F0.wireOp",EDGE,"E104.MirrorCS");var subQ2=makeQuery(id+"F0.imprint","INTERSECT",VERTEX,{"derivedFrom":[subQ1,subQ0]});Q68=makeQuery(id+"F0.imprint","IMPRINT",FACE,{"disambiguationData":[TD([[makeQuery(id+"F0.imprint","IMPRINT",EDGE,{"disambiguationData":[TD([[subQ2,-1.0]])],"derivedFrom":subQ1}),-1.0]])]});}
            var Q69;
            {var subQ0=sQuery(id+"F0.wireOp",EDGE,"E101.MirrorCS");var subQ1=sQuery(id+"F0.wireOp",EDGE,"E98.MirrorC");var subQ2=makeQuery(id+"F0.imprint","INTERSECT",VERTEX,{"derivedFrom":[subQ1,subQ0]});Q69=makeQuery(id+"F0.imprint","IMPRINT",FACE,{"disambiguationData":[TD([[makeQuery(id+"F0.imprint","IMPRINT",EDGE,{"disambiguationData":[TD([[subQ2,-1.0]])],"derivedFrom":subQ1}),1.0]])]});}
            var Q70;
            {var subQ0=sQuery(id+"F0.wireOp",EDGE,"E100.MirrorCS");var subQ1=sQuery(id+"F0.wireOp",EDGE,"E97.MirrorC");var subQ2=makeQuery(id+"F0.imprint","INTERSECT",VERTEX,{"derivedFrom":[subQ1,subQ0]});Q70=makeQuery(id+"F0.imprint","IMPRINT",FACE,{"disambiguationData":[TD([[makeQuery(id+"F0.imprint","IMPRINT",EDGE,{"disambiguationData":[TD([[subQ2,1.0]])],"derivedFrom":subQ1}),1.0]])]});}
            var Q71;
            {var subQ0=sQuery(id+"F0.wireOp",EDGE,"E100.MirrorCS");var subQ1=sQuery(id+"F0.wireOp",EDGE,"E99.MirrorC");var subQ2=makeQuery(id+"F0.imprint","INTERSECT",VERTEX,{"derivedFrom":[subQ1,subQ0]});Q71=makeQuery(id+"F0.imprint","IMPRINT",FACE,{"disambiguationData":[TD([[makeQuery(id+"F0.imprint","IMPRINT",EDGE,{"disambiguationData":[TD([[subQ2,-1.0]])],"derivedFrom":subQ1}),1.0]])]});}
            extrude(context, id + "F1", {"entities" : qUnion([Q0, Q1, Q2, Q3, Q4, Q5, Q6, Q7, Q8, Q9, Q10, Q11, Q12, Q13, Q14, Q15, Q16, Q17, Q18, Q19, Q20, Q21, Q22, Q23, Q24, Q25, Q26, Q27, Q28, Q29, Q30, Q31, Q32, Q33, Q34, Q35, Q36, Q37, Q38, Q39, Q40, Q41, Q42, Q43, Q44, Q45, Q46, Q47, Q48, Q49, Q50, Q51, Q52, Q53, Q54, Q55, Q56, Q57, Q58, Q59, Q60, Q61, Q62, Q63, Q64, Q65, Q66, Q67, Q68, Q69, Q70, Q71]), "depth" : 3 * mm, "offsetDistance" : 25 * mm});
        }
    });
